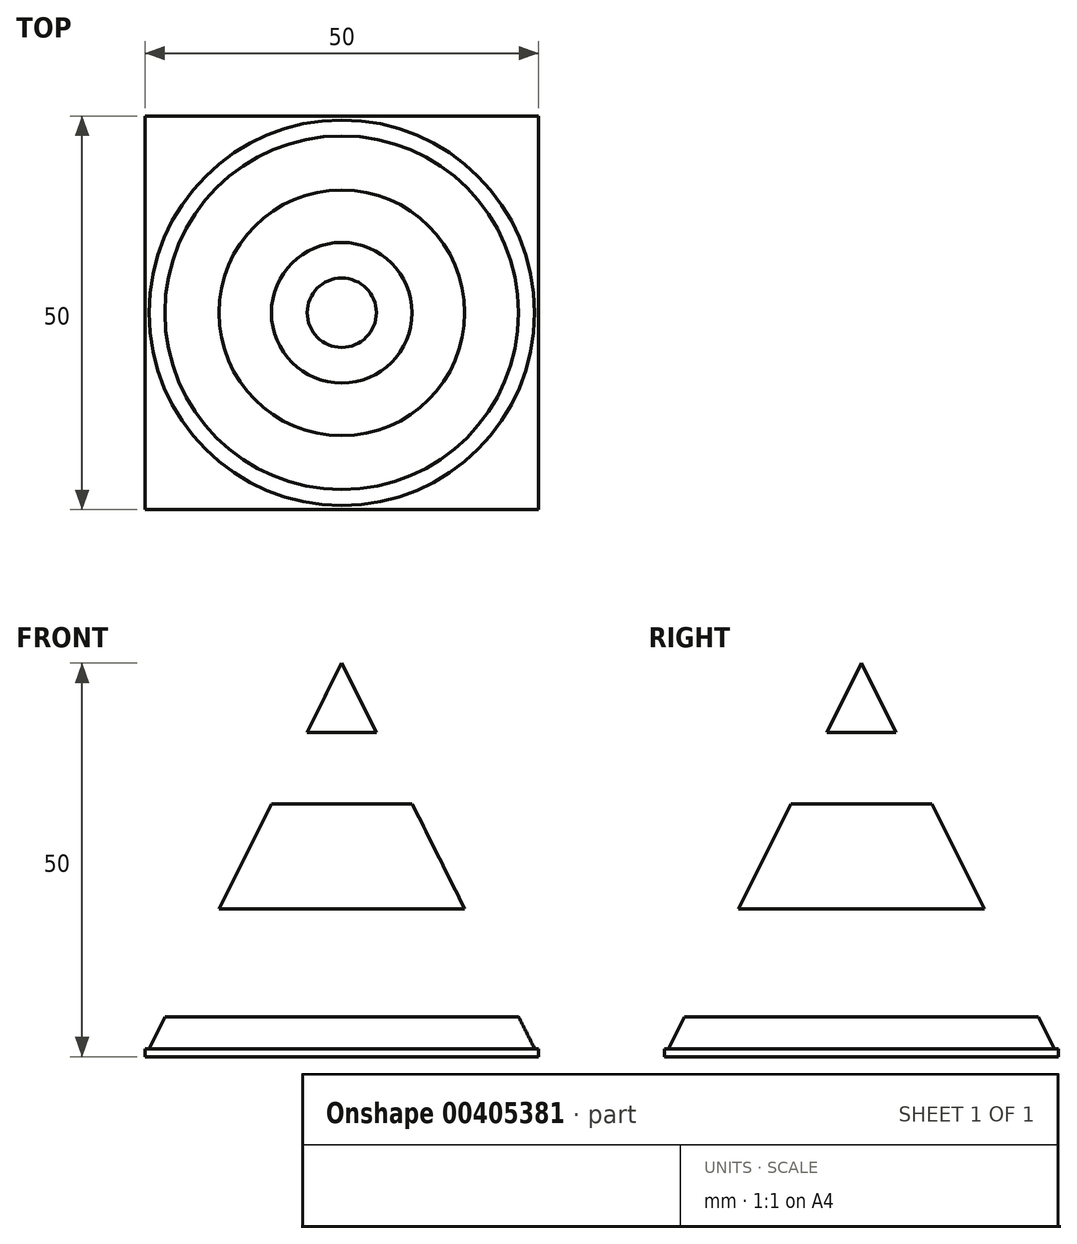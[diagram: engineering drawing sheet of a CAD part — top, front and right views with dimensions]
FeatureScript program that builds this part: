
annotation { "Feature Type Name" : "Feature", "Feature Type Description" : "" }
export const myFeature = defineFeature(function(context is Context, id is Id, definition is map)
    precondition{}
    {
        {
            var Q0;
            Q0=qCreatedBy(makeId("Front.planeOp"),FACE);
            var sketch = newSketch(context, id + "F0", { "sketchPlane" : qUnion([Q0])});
            skLineSegment(sketch, "E0.top", {"start": v(0, 0) * mm, "end": v(25, 0) * mm});
            skLineSegment(sketch, "E0.left", {"start": v(0, 50) * mm, "end": v(0, 41.2) * mm});
            skLineSegment(sketch, "E1", {"start": v(0, 50) * mm, "end": v(4.4, 41.2) * mm});
            skLineSegment(sketch, "E2.bottom", {"start": v(0, 41.2) * mm, "end": v(4.4, 41.2) * mm});
            skLineSegment(sketch, "E2.top", {"start": v(0, 32.13) * mm, "end": v(8.94, 32.13) * mm});
            skLineSegment(sketch, "E3.bottom", {"start": v(0, 18.78) * mm, "end": v(15.6, 18.78) * mm});
            skLineSegment(sketch, "E3.top", {"start": v(0, 5.07) * mm, "end": v(22.47, 5.07) * mm});
            skLineSegment(sketch, "E4.trimOffspring", {"start": v(8.94, 32.13) * mm, "end": v(15.6, 18.78) * mm});
            skLineSegment(sketch, "E5.trimOffspring", {"start": v(0, 32.13) * mm, "end": v(0, 18.78) * mm});
            skLineSegment(sketch, "E6.trimOffspring", {"start": v(22.47, 5.07) * mm, "end": v(25, 0) * mm});
            skLineSegment(sketch, "E7.trimOffspring", {"start": v(0, 5.07) * mm, "end": v(0, 0) * mm});
            skSolve(sketch);
        }
        {
            var Q0;
            Q0 = qSketchRegion(id + "F0", true);
            var Q1;
            Q1=sQuery(id+"F0.wireOp",EDGE,"E5.trimOffspring");
            revolve(context, id + "F1", {"entities" : qUnion([Q0]), "axis" : qUnion([Q1]), "revolveType" : RevolveType.FULL});
        }
        {
            var Q0;
            Q0=qCreatedBy(makeId("Top.planeOp"),FACE);
            var sketch = newSketch(context, id + "F2", { "sketchPlane" : qUnion([Q0])});
            skLineSegment(sketch, "E8.bottom", {"start": v(-25, 25) * mm, "end": v(25, 25) * mm});
            skLineSegment(sketch, "E8.top", {"start": v(-25, -25) * mm, "end": v(25, -25) * mm});
            skLineSegment(sketch, "E8.left", {"start": v(-25, 25) * mm, "end": v(-25, -25) * mm});
            skLineSegment(sketch, "E8.right", {"start": v(25, 25) * mm, "end": v(25, -25) * mm});
            skSolve(sketch);
        }
        {
            var Q0;
            Q0=makeQuery(id+"F2.imprint","IMPRINT",FACE,{"disambiguationData":[TD([[makeQuery(id+"F2.imprint","IMPRINT",EDGE,{"derivedFrom":sQuery(id+"F2.wireOp",EDGE,"E8.bottom")}),-1.0]])]});
            extrude(context, id + "F3", {"entities" : qUnion([Q0]), "operationType" : NewBodyOperationType.ADD, "depth" : 1 * mm});
        }
    });
